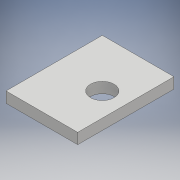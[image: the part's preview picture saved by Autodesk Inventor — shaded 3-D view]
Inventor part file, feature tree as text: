
AUTODESK INVENTOR PART (.ipt)
format: ipt  version: 2017 SP1 (Build 210196100, 196)  size: 99,328 bytes
history: native  units: mm
features: extrude x2, sketch x2
ambient origin geometry x8: Origin, YZ Plane, XZ Plane, XY Plane, X Axis, Y Axis, Z Axis, Center Point
bodies: Solide1 (feature_tree)
feature tree (4):
  extrude  "Extrusion1"  Depth=90.0mm
  extrude  "Extrusion2"  Depth=67.0mm
  sketch  "Esquisse1"
  sketch  "Esquisse2"
